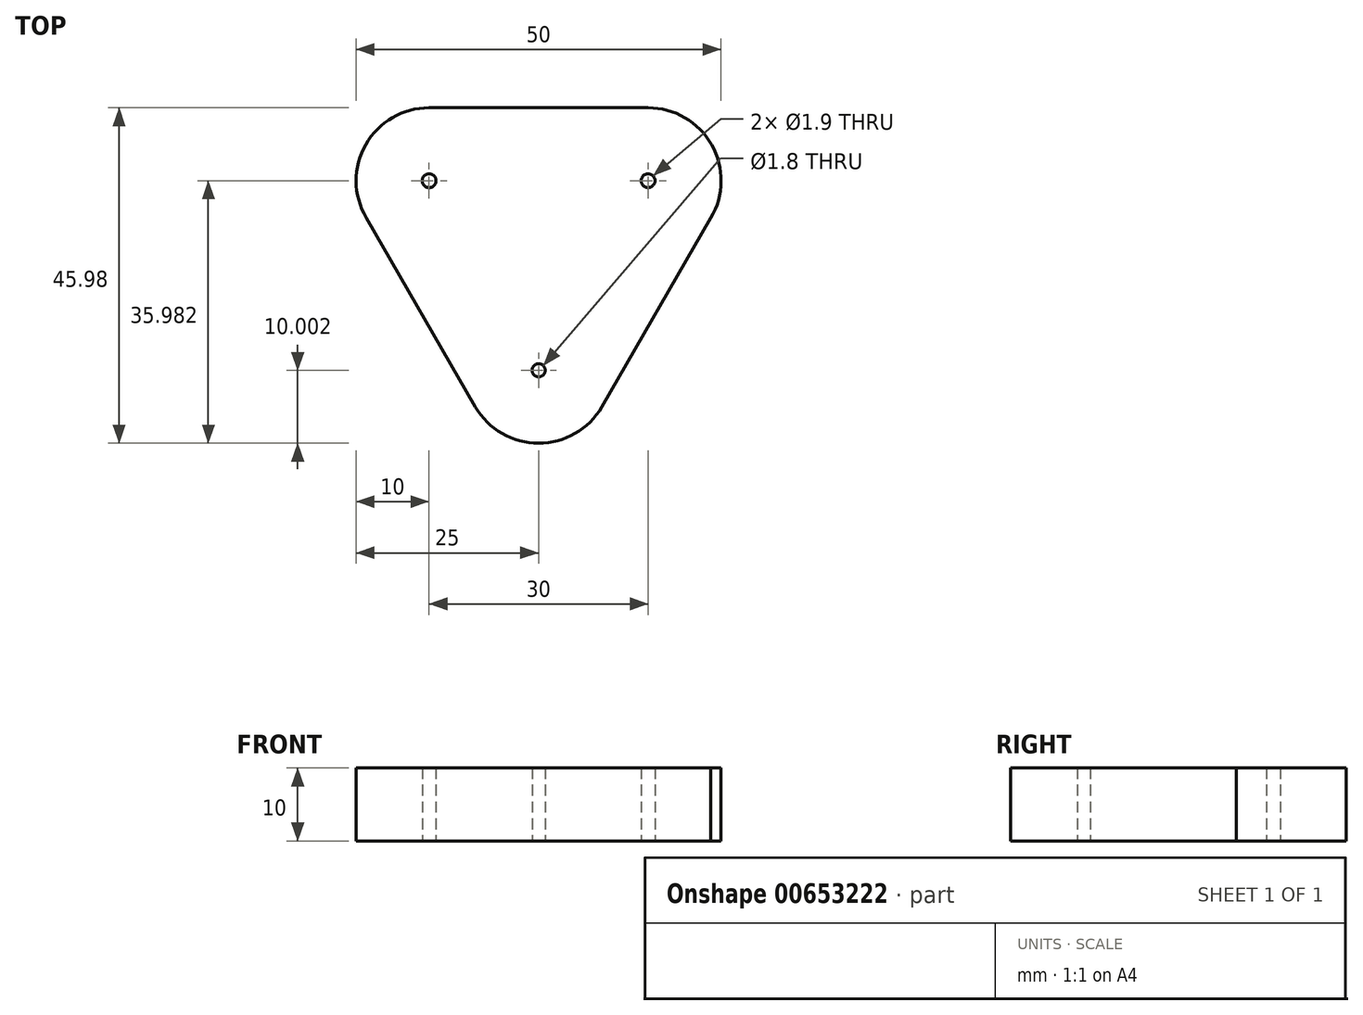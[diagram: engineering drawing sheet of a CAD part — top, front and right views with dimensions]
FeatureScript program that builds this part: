
annotation { "Feature Type Name" : "Feature", "Feature Type Description" : "" }
export const myFeature = defineFeature(function(context is Context, id is Id, definition is map)
    precondition{}
    {
        {
            var Q0;
            Q0=qCreatedBy(makeId("Top.planeOp"),FACE);
            var sketch = newSketch(context, id + "F0", { "sketchPlane" : qUnion([Q0])});
            skArc(sketch, "E0", {"start": v(0, 49.35) * mm, "mid": v(-8.68, 44.32) * mm, "end": v(-8.62, 34.28) * mm});
            skArc(sketch, "E1", {"start": v(38.6, 34.25) * mm, "mid": v(38.7, 44.3) * mm, "end": v(30, 49.35) * mm});
            skArc(sketch, "E2", {"start": v(6.34, 8.37) * mm, "mid": v(15, 3.37) * mm, "end": v(23.66, 8.37) * mm});
            skLineSegment(sketch, "E3", {"start": v(38.72, 34.46) * mm, "end": v(23.66, 8.37) * mm});
            skLineSegment(sketch, "E4", {"start": v(-8.7, 34.43) * mm, "end": v(6.34, 8.37) * mm});
            skLineSegment(sketch, "E5", {"start": v(0, 49.35) * mm, "end": v(30, 49.35) * mm});
            skCircle(sketch, "E6", {"center": v(0, 39.35) * mm, "radius": 0.95 * mm});
            skCircle(sketch, "E7", {"center": v(30, 39.35) * mm, "radius": 0.95 * mm});
            skCircle(sketch, "E8", {"center": v(15, 13.37) * mm, "radius": 0.9 * mm});
            skSolve(sketch);
        }
        {
            var Q0;
            Q0 = qSketchRegion(id + "F0", true);
            extrude(context, id + "F1", {"entities" : qUnion([Q0]), "depth" : 10 * mm, "offsetDistance" : 25 * mm});
        }
    });
